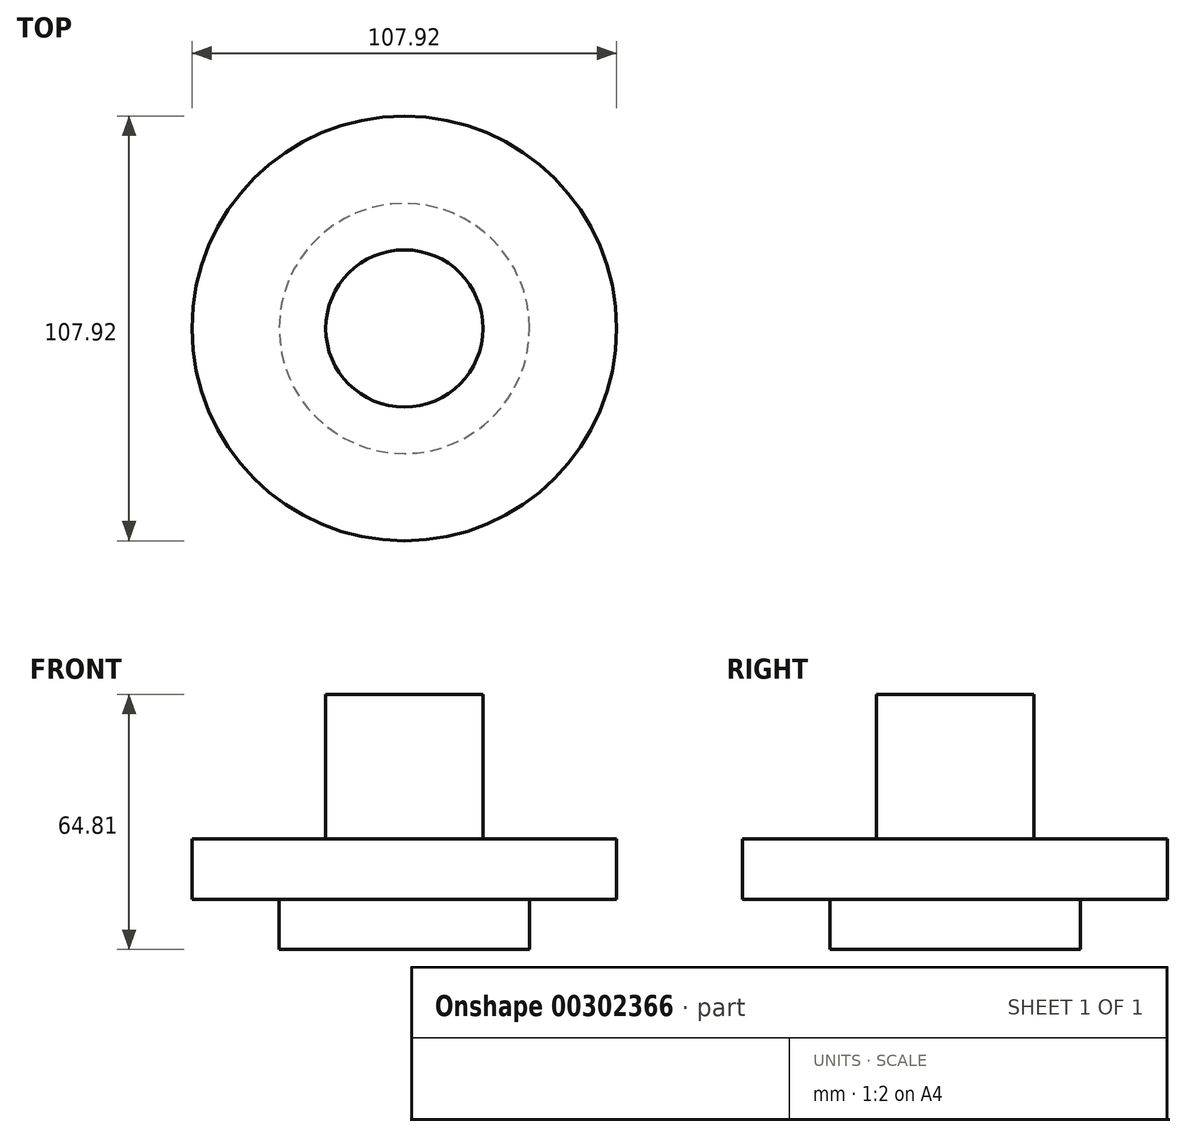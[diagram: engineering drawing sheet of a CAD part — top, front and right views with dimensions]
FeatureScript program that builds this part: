
annotation { "Feature Type Name" : "Feature", "Feature Type Description" : "" }
export const myFeature = defineFeature(function(context is Context, id is Id, definition is map)
    precondition{}
    {
        {
            var Q0;
            Q0=qCreatedBy(makeId("Front.planeOp"),FACE);
            var sketch = newSketch(context, id + "F0", { "sketchPlane" : qUnion([Q0])});
            skLineSegment(sketch, "E0", {"start": v(0, 0) * mm, "end": v(-31.8, 0) * mm});
            skLineSegment(sketch, "E1", {"start": v(-31.8, 0) * mm, "end": v(-31.8, 12.67) * mm});
            skLineSegment(sketch, "E2", {"start": v(-31.8, 12.67) * mm, "end": v(-53.96, 12.67) * mm});
            skLineSegment(sketch, "E3", {"start": v(-53.96, 12.67) * mm, "end": v(-53.96, 28.11) * mm});
            skLineSegment(sketch, "E4", {"start": v(-53.96, 28.11) * mm, "end": v(-19.97, 28.11) * mm});
            skLineSegment(sketch, "E5", {"start": v(-19.97, 28.11) * mm, "end": v(-19.97, 64.8) * mm});
            skLineSegment(sketch, "E6", {"start": v(-19.97, 64.8) * mm, "end": v(0, 64.8) * mm});
            skLineSegment(sketch, "E7", {"start": v(0, 64.8) * mm, "end": v(0, 0) * mm});
            skSolve(sketch);
        }
        {
            var Q0;
            Q0=makeQuery(id+"F0.imprint","IMPRINT",FACE,{"disambiguationData":[TD([[makeQuery(id+"F0.imprint","IMPRINT",EDGE,{"derivedFrom":sQuery(id+"F0.wireOp",EDGE,"E0")}),-1.0]])]});
            var Q1;
            Q1=sQuery(id+"F0.wireOp",EDGE,"E7");
            revolve(context, id + "F1", {"entities" : qUnion([Q0]), "axis" : qUnion([Q1]), "revolveType" : RevolveType.FULL});
        }
    });
